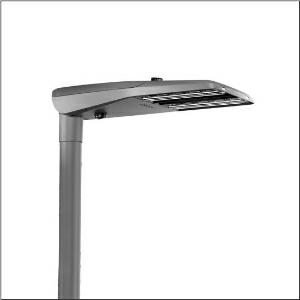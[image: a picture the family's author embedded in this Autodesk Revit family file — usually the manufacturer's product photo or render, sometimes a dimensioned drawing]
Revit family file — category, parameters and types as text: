
# Revit family: streetlight_sl_11_iq_midi___pc-r_5xc3f51y08me_63e7
name_source: partatom
category: Lighting Fixtures
units: mm (PartAtom-declared; Revit-internal decimal feet)

## family parameters
Cut with Voids When Loaded = No
Host = Face
Light Source = No
Part Type = Normal
Room Calculation Point = No
Round Connector Dimension = Use Diameter
Shared = No

## types (1)
- --- (1 x LED, 15540 lm, 122.7 W, 3000K)
    Apparent Load = 123 VA
    CIE Flux Codes = 37 73 96 100 100
    Color Rendering = 70
    Color Temperature = 3000K
    Default Elevation = 1800 mm
    Description = Streetlight SL 11 iQ midi, mast luminaire, primary light control with 3 zone facetted reflector, of plastic, silver coated, highly specular, primary optical cover: cover, of PMMA, transparent, light distribution: PC-R, light emission: direct distribution, primary light characteristic: asymmetric, right, installation type: post-top, side-entry, LED, High Power LED, rated luminous flux: 15.540lm, luminous efficacy: 126lm/W, light colour: 730, colour temperature: 3000K, control: presetting dimming logarithmic, Street-Remote, Auto-Match, Temp-Guard, Lumen-Switch, Night-Set, Smart-Wire, Light-Fading, Desk-Remote (wireless, voltage-free reading and setting of iQ features in the workshop via application-optimized NFC function/RFID function), optimised constant luminous flux control (CLO 2.0), with cable H07RN-F 5x 1.5mm², mains connection: 220..240V, AC, 50/60Hz, connection cable pre-assembled, cable length: 12,5m, start of lifetime: 123W, end of service life: 130W, reduction: 56W, luminaire housing, of diecast aluminium, powder-coated, Siteco® metallic grey (DB 702S), please order mast flange separately, inclination adjustable without tools: 0°, 5°, 10°, 15° (post-top) | 0°, -5°, -10°, -15° (side-entry), sealing non-destructively replaceable, multi-level sealing system, length: 780mm, width: 376mm, height: 118mm, spigot size: 60/76mm (post-top) and 42/60/76mm (side-entry), mast flange for spigot size: 42mm: 5XC10008XM4, 60mm: 5XC10008XM2, 76/60mm: 5XC10108XM1, equipment: Power, Smart Interface below and above, protection rating (complete): IP66, insulation class (complete): insulation class II (safety insulation), certification: CE, ENEC in preparation, impact resistance: IK09, permissible operating ambient temperature for outdoor applications: -25..+50°C, standard-compliant lighting for roads and squares, packaging unit: 1 piece

Light Distribution: PC-R
    Height = 118 mm
    Lamp = 1 x LED
    Lamp Light Flux = 15540 lm
    Lamp Power = 122.7 W
    Lamp count = 1
    Length = 780 mm
    Luminous efficacy = 127 lm/W
    Manufacturer = Siteco
    ModVariant = No
    Model = 5XC3F51Y08ME
    Number of Poles = 1
    OnlyDefault = Yes
    Power Factor = 1
    Product Name = Streetlight SL 11 iQ midi | PC-R
    Product group = mast luminaire | pylon top
    ProductGroupID = 6100
    Protection Class = Protection class II
    Protection Degree = IP 66
    RLX_Detail_Level = 1
    RlxData = <blob elided: 73441 chars, md5=3d56e740>
    Socket = socket
    Standby Power = 0 W
    System Light Flux = 15540 lm
    System Power = 123 W
    Type Comments = factory setting: luminous flux: 100 % | dim-lin: 254 | 552 mA
    Type Image = l_1004429.jpg
    URL = http://relux.com
    VarID = @adj_043353
    Voltage = 0 V
    Weight = 0.00 kg
    Width = 376 mm

## geometry (parser evidence)
native form markers: Blend x4, Sweep x12
no freeform markers — native parametric forms only
